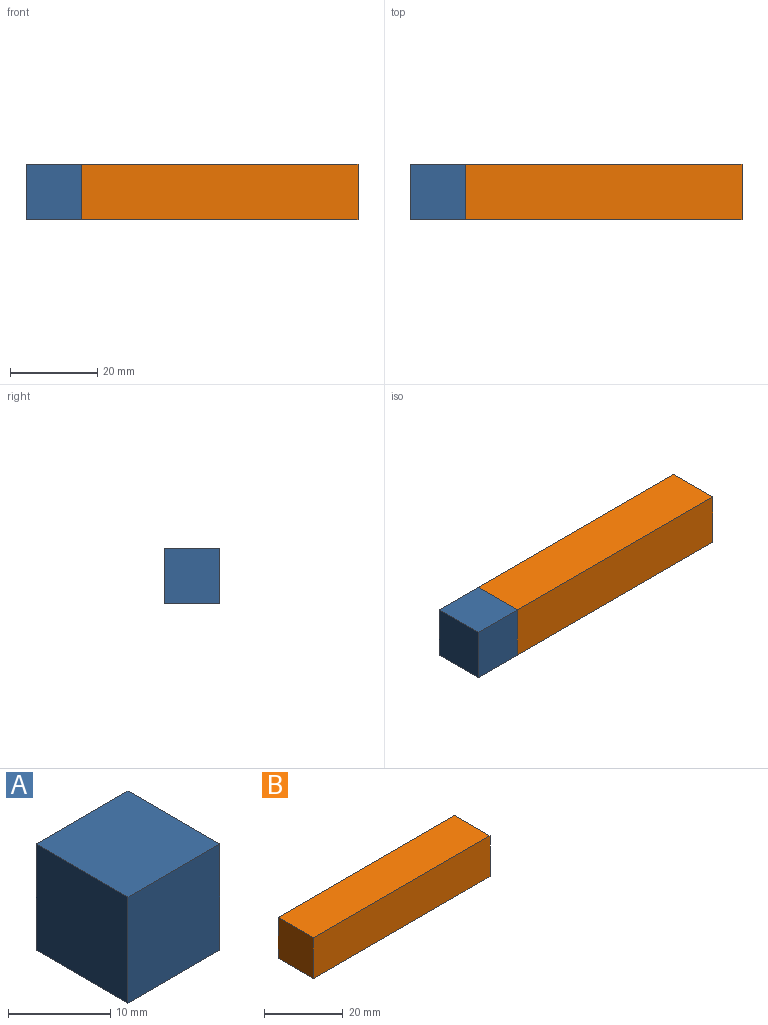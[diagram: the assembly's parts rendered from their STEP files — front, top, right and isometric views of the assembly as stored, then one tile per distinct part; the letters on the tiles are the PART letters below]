
ASSEMBLY  parts=2 mates=1
PART A: 6 faces, bbox 12.7x12.7x12.7 mm
  f0: plane 12.7x12.7mm, normal (0,0,-1), area 161.3mm2, adj f1,f3,f4,f5
  f1: plane 12.7x12.7mm, normal (1,0,0), area 161.3mm2, adj f0,f2,f4,f5
  f2: plane 12.7x12.7mm, normal (0,0,1), area 161.3mm2, adj f1,f3,f4,f5
  f3: plane 12.7x12.7mm, normal (-1,0,0), area 161.3mm2, adj f0,f2,f4,f5
  f4: plane 12.7x12.7mm, normal (0,-1,0), area 161.3mm2, adj f0,f1,f2,f3
  f5: plane 12.7x12.7mm, normal (0,1,0), area 161.3mm2, adj f0,f1,f2,f3
PART B: 6 faces, bbox 63.5x12.7x12.7 mm
  f0: plane 63.5x12.7mm, normal (0,0,-1), area 806.5mm2, adj f1,f3,f4,f5
  f1: plane 12.7x12.7mm, normal (1,0,0), area 161.3mm2, adj f0,f2,f4,f5
  f2: plane 63.5x12.7mm, normal (0,0,1), area 806.5mm2, adj f1,f3,f4,f5
  f3: plane 12.7x12.7mm, normal (-1,0,0), area 161.3mm2, adj f0,f2,f4,f5
  f4: plane 63.5x12.7mm, normal (0,-1,0), area 806.5mm2, adj f0,f1,f2,f3
  f5: plane 63.5x12.7mm, normal (0,1,0), area 806.5mm2, adj f0,f1,f2,f3
PLACE A t=(-33.41,14.04,-40.95)mm
PLACE B t=(8,14.04,31.23)mm
MATE slider A.f1 <-> B.f3  axis (1,0,0) through (-27.06,7.69,-12.38)mm
